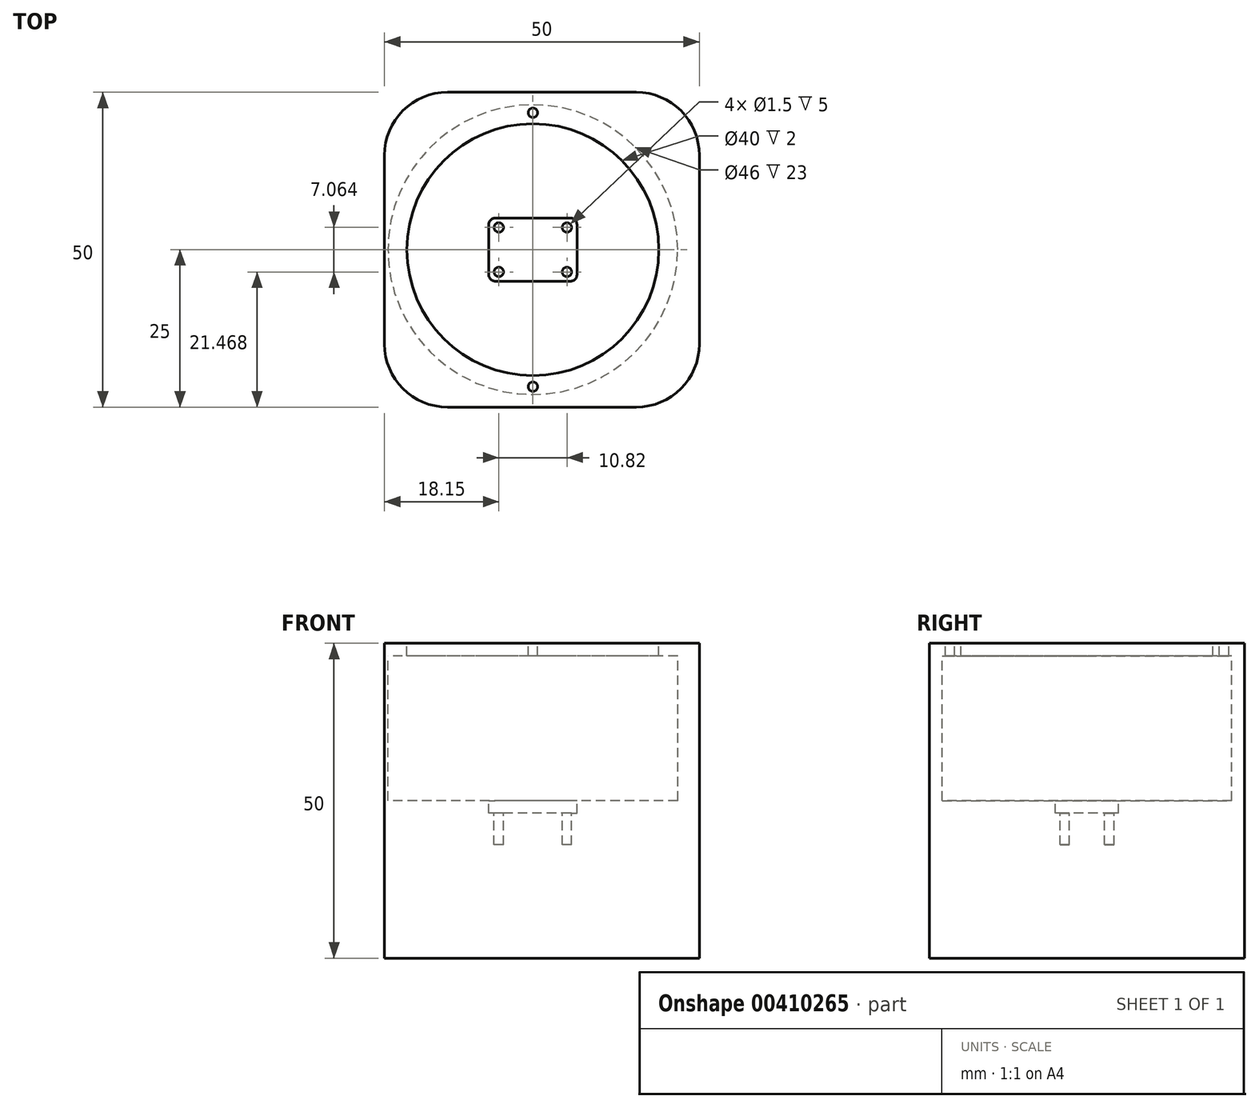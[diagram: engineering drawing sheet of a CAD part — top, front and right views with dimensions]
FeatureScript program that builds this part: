
annotation { "Feature Type Name" : "Feature", "Feature Type Description" : "" }
export const myFeature = defineFeature(function(context is Context, id is Id, definition is map)
    precondition{}
    {
        {
            var Q0;
            Q0=qCreatedBy(makeId("Top.planeOp"),FACE);
            var sketch = newSketch(context, id + "F0", { "sketchPlane" : qUnion([Q0])});
            skLineSegment(sketch, "E0.bottom", {"start": v(-13.56, 25) * mm, "end": v(16.44, 25) * mm});
            skLineSegment(sketch, "E0.top", {"start": v(-13.56, -25) * mm, "end": v(16.44, -25) * mm});
            skLineSegment(sketch, "E0.left", {"start": v(-23.56, 15) * mm, "end": v(-23.56, -15) * mm});
            skLineSegment(sketch, "E0.right", {"start": v(26.44, 15) * mm, "end": v(26.44, -15) * mm});
            skPoint(sketch, "E1.visualSharp", {"position": v(-23.56, 25) * mm});
            skArc(sketch, "E1.filletArc", {"start": v(-13.56, 25) * mm, "mid": v(-20.63, 22.07) * mm, "end": v(-23.56, 15) * mm});
            skPoint(sketch, "E2.visualSharp", {"position": v(26.44, 25) * mm});
            skArc(sketch, "E2.filletArc", {"start": v(26.44, 15) * mm, "mid": v(23.5, 22.07) * mm, "end": v(16.44, 25) * mm});
            skPoint(sketch, "E3.visualSharp", {"position": v(-23.56, -25) * mm});
            skArc(sketch, "E3.filletArc", {"start": v(-23.56, -15) * mm, "mid": v(-20.63, -22.07) * mm, "end": v(-13.56, -25) * mm});
            skPoint(sketch, "E4.visualSharp", {"position": v(26.44, -25) * mm});
            skArc(sketch, "E4.filletArc", {"start": v(16.44, -25) * mm, "mid": v(23.5, -22.07) * mm, "end": v(26.44, -15) * mm});
            skSolve(sketch);
        }
        {
            var Q0;
            Q0=makeQuery(id+"F0.imprint","IMPRINT",FACE,{"disambiguationData":[TD([[makeQuery(id+"F0.imprint","IMPRINT",EDGE,{"derivedFrom":sQuery(id+"F0.wireOp",EDGE,"E0.bottom")}),-1.0]])]});
            extrude(context, id + "F1", {"entities" : qUnion([Q0]), "depth" : 50 * mm});
        }
        {
            var Q0;
            Q0=makeQuery(id+"F1.opExtrude","CAP_FACE",FACE,{"disambiguationData":[OSD([sQuery(id+"F0.wireOp",EDGE,"E0.bottom"),sQuery(id+"F0.wireOp",EDGE,"E0.top"),sQuery(id+"F0.wireOp",EDGE,"E0.left"),sQuery(id+"F0.wireOp",EDGE,"E0.right"),sQuery(id+"F0.wireOp",EDGE,"E1.filletArc"),sQuery(id+"F0.wireOp",EDGE,"E2.filletArc"),sQuery(id+"F0.wireOp",EDGE,"E3.filletArc"),sQuery(id+"F0.wireOp",EDGE,"E4.filletArc")])],"isStart":false});
            var sketch = newSketch(context, id + "F2", { "sketchPlane" : qUnion([Q0])});
            skCircle(sketch, "E5", {"center": v(0, 0) * mm, "radius": 20 * mm});
            skSolve(sketch);
        }
        {
            var Q0;
            Q0=makeQuery(id+"F2.imprint","IMPRINT",FACE,{"disambiguationData":[TD([[makeQuery(id+"F2.imprint","IMPRINT",EDGE,{"derivedFrom":sQuery(id+"F2.wireOp",EDGE,"E5")}),1.0]])]});
            extrude(context, id + "F3", {"entities" : qUnion([Q0]), "operationType" : NewBodyOperationType.REMOVE, "oppositeDirection" : true, "depth" : 25 * mm});
        }
        {
            var Q0;
            Q0=qCreatedBy(makeId("Front.planeOp"),FACE);
            var sketch = newSketch(context, id + "F4", { "sketchPlane" : qUnion([Q0])});
            skLineSegment(sketch, "E6", {"start": v(20, 50) * mm, "end": v(20, 48) * mm});
            skLineSegment(sketch, "E7", {"start": v(20, 48) * mm, "end": v(23, 48) * mm});
            skLineSegment(sketch, "E8", {"start": v(23, 48) * mm, "end": v(23, 25) * mm});
            skLineSegment(sketch, "E9", {"start": v(23, 25) * mm, "end": v(0, 25) * mm});
            skLineSegment(sketch, "E10", {"start": v(0, 25) * mm, "end": v(0, 50) * mm});
            skLineSegment(sketch, "E11", {"start": v(0, 50) * mm, "end": v(20, 50) * mm});
            skSolve(sketch);
        }
        {
            var Q0;
            Q0 = qSketchRegion(id + "F4", true);
            var Q1;
            Q1=sQuery(id+"F4.wireOp",EDGE,"E10");
            revolve(context, id + "F5", {"operationType" : NewBodyOperationType.REMOVE, "entities" : qUnion([Q0]), "axis" : qUnion([Q1]), "revolveType" : RevolveType.FULL, "oppositeDirection" : true});
        }
        {
            var Q0;
            Q0=makeQuery(id+"F1.opExtrude","CAP_FACE",FACE,{"disambiguationData":[OSD([sQuery(id+"F0.wireOp",EDGE,"E0.bottom"),sQuery(id+"F0.wireOp",EDGE,"E0.top"),sQuery(id+"F0.wireOp",EDGE,"E0.left"),sQuery(id+"F0.wireOp",EDGE,"E0.right"),sQuery(id+"F0.wireOp",EDGE,"E1.filletArc"),sQuery(id+"F0.wireOp",EDGE,"E2.filletArc"),sQuery(id+"F0.wireOp",EDGE,"E3.filletArc"),sQuery(id+"F0.wireOp",EDGE,"E4.filletArc")])],"isStart":false});
            var sketch = newSketch(context, id + "F6", { "sketchPlane" : qUnion([Q0])});
            skCircle(sketch, "E12", {"center": v(0, 21.75) * mm, "radius": 0.75 * mm});
            skCircle(sketch, "E13.MirrorC", {"center": v(0, -21.75) * mm, "radius": 0.75 * mm});
            skSolve(sketch);
        }
        {
            var Q0;
            Q0 = qSketchRegion(id + "F6", true);
            extrude(context, id + "F7", {"entities" : qUnion([Q0]), "operationType" : NewBodyOperationType.REMOVE, "oppositeDirection" : true, "depth" : 25 * mm});
        }
        {
            var Q0;
            Q0=makeQuery(id+"F5.boolean.opBoolean","MERGE",FACE,{"derivedFrom":[makeQuery(id+"F3.boolean.opBoolean","COPY",FACE,{"derivedFrom":makeQuery(id+"F3.opExtrude","CAP_FACE",FACE,{"disambiguationData":[OSD([sQuery(id+"F2.wireOp",EDGE,"E5")])],"isStart":false})}),makeQuery(id+"F5.opRevolve","SWEPT_FACE",FACE,{"disambiguationData":[OSD([sQuery(id+"F4.wireOp",EDGE,"E9")])]})]});
            var sketch = newSketch(context, id + "F8", { "sketchPlane" : qUnion([Q0])});
            skLineSegment(sketch, "E14.bottom", {"start": v(6, 5) * mm, "end": v(-6, 5) * mm});
            skLineSegment(sketch, "E14.top", {"start": v(6, -5) * mm, "end": v(-6, -5) * mm});
            skLineSegment(sketch, "E14.left", {"start": v(7, 4) * mm, "end": v(7, -4) * mm});
            skLineSegment(sketch, "E14.right", {"start": v(-7, 4) * mm, "end": v(-7, -4) * mm});
            skPoint(sketch, "E14.middle", {"position": v(0, 0) * mm});
            skPoint(sketch, "E15.visualSharp", {"position": v(-7, 5) * mm});
            skArc(sketch, "E15.filletArc", {"start": v(-6, 5) * mm, "mid": v(-6.7, 4.7) * mm, "end": v(-7, 4) * mm});
            skPoint(sketch, "E16.visualSharp", {"position": v(7, 5) * mm});
            skArc(sketch, "E16.filletArc", {"start": v(7, 4) * mm, "mid": v(6.7, 4.7) * mm, "end": v(6, 5) * mm});
            skPoint(sketch, "E17.visualSharp", {"position": v(-7, -5) * mm});
            skArc(sketch, "E17.filletArc", {"start": v(-7, -4) * mm, "mid": v(-6.7, -4.7) * mm, "end": v(-6, -5) * mm});
            skPoint(sketch, "E18.visualSharp", {"position": v(7, -5) * mm});
            skArc(sketch, "E18.filletArc", {"start": v(6, -5) * mm, "mid": v(6.7, -4.7) * mm, "end": v(7, -4) * mm});
            skSolve(sketch);
        }
        {
            var Q0;
            Q0 = qSketchRegion(id + "F8", true);
            extrude(context, id + "F9", {"entities" : qUnion([Q0]), "operationType" : NewBodyOperationType.REMOVE, "oppositeDirection" : true, "depth" : 2 * mm});
        }
        {
            var Q0;
            Q0=makeQuery(id+"F9.boolean.opBoolean","COPY",FACE,{"derivedFrom":makeQuery(id+"F9.opExtrude","CAP_FACE",FACE,{"disambiguationData":[OSD([sQuery(id+"F8.wireOp",EDGE,"E14.bottom"),sQuery(id+"F8.wireOp",EDGE,"E14.top"),sQuery(id+"F8.wireOp",EDGE,"E14.left"),sQuery(id+"F8.wireOp",EDGE,"E14.right"),sQuery(id+"F8.wireOp",EDGE,"E15.filletArc"),sQuery(id+"F8.wireOp",EDGE,"E16.filletArc"),sQuery(id+"F8.wireOp",EDGE,"E17.filletArc"),sQuery(id+"F8.wireOp",EDGE,"E18.filletArc")])],"isStart":false})});
            var sketch = newSketch(context, id + "F10", { "sketchPlane" : qUnion([Q0])});
            skCircle(sketch, "E19", {"center": v(-5.41, 3.53) * mm, "radius": 0.75 * mm});
            skCircle(sketch, "E20.MirrorC", {"center": v(-5.41, -3.53) * mm, "radius": 0.75 * mm});
            skCircle(sketch, "E21.MirrorC", {"center": v(5.41, 3.53) * mm, "radius": 0.75 * mm});
            skCircle(sketch, "E22.MirrorC", {"center": v(5.41, -3.53) * mm, "radius": 0.75 * mm});
            skSolve(sketch);
        }
        {
            var Q0;
            Q0 = qSketchRegion(id + "F10", true);
            extrude(context, id + "F11", {"entities" : qUnion([Q0]), "operationType" : NewBodyOperationType.REMOVE, "oppositeDirection" : true, "depth" : 5 * mm});
        }
        {
            var Q0;
            Q0=makeQuery(id+"F1.opExtrude","SWEPT_FACE",FACE,{"disambiguationData":[OSD([sQuery(id+"F0.wireOp",EDGE,"E0.top")])]});
            var sketch = newSketch(context, id + "F12", { "sketchPlane" : qUnion([Q0])});
            skCircle(sketch, "E23", {"center": v(0, 25.9) * mm, "radius": 1.25 * mm});
            skSolve(sketch);
        }
        {
            var Q0;
            Q0=sQuery(id+"F12.wireOp",EDGE,"E23");
            extrude(context, id + "F13", {"bodyType" : ToolBodyType.SURFACE, "surfaceEntities" : qUnion([Q0]), "depth" : 25 * mm});
        }
    });
